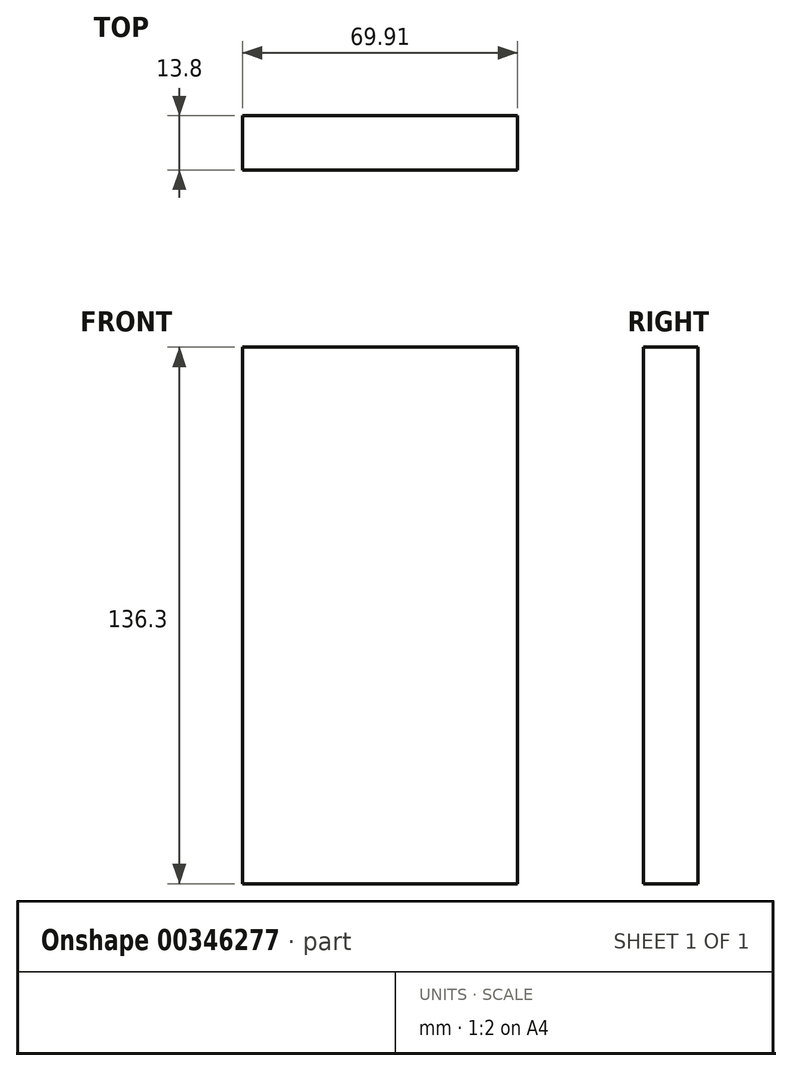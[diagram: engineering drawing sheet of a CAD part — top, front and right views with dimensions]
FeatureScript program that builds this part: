
annotation { "Feature Type Name" : "Feature", "Feature Type Description" : "" }
export const myFeature = defineFeature(function(context is Context, id is Id, definition is map)
    precondition{}
    {
        {
            var Q0;
            Q0=qCreatedBy(makeId("Front.planeOp"),FACE);
            var sketch = newSketch(context, id + "F0", { "sketchPlane" : qUnion([Q0])});
            skLineSegment(sketch, "E0.bottom", {"start": v(27.27, -19.8) * mm, "end": v(-42.64, -19.8) * mm});
            skLineSegment(sketch, "E0.top", {"start": v(27.27, 116.5) * mm, "end": v(-42.64, 116.5) * mm});
            skLineSegment(sketch, "E0.left", {"start": v(27.27, -19.8) * mm, "end": v(27.27, 116.5) * mm});
            skLineSegment(sketch, "E0.right", {"start": v(-42.64, -19.8) * mm, "end": v(-42.64, 116.5) * mm});
            skPoint(sketch, "E0.middle", {"position": v(-7.68, 48.36) * mm});
            skSolve(sketch);
        }
        {
            var Q0;
            Q0 = qSketchRegion(id + "F0", true);
            extrude(context, id + "F1", {"entities" : qUnion([Q0]), "depth" : 13.8 * mm});
        }
    });
